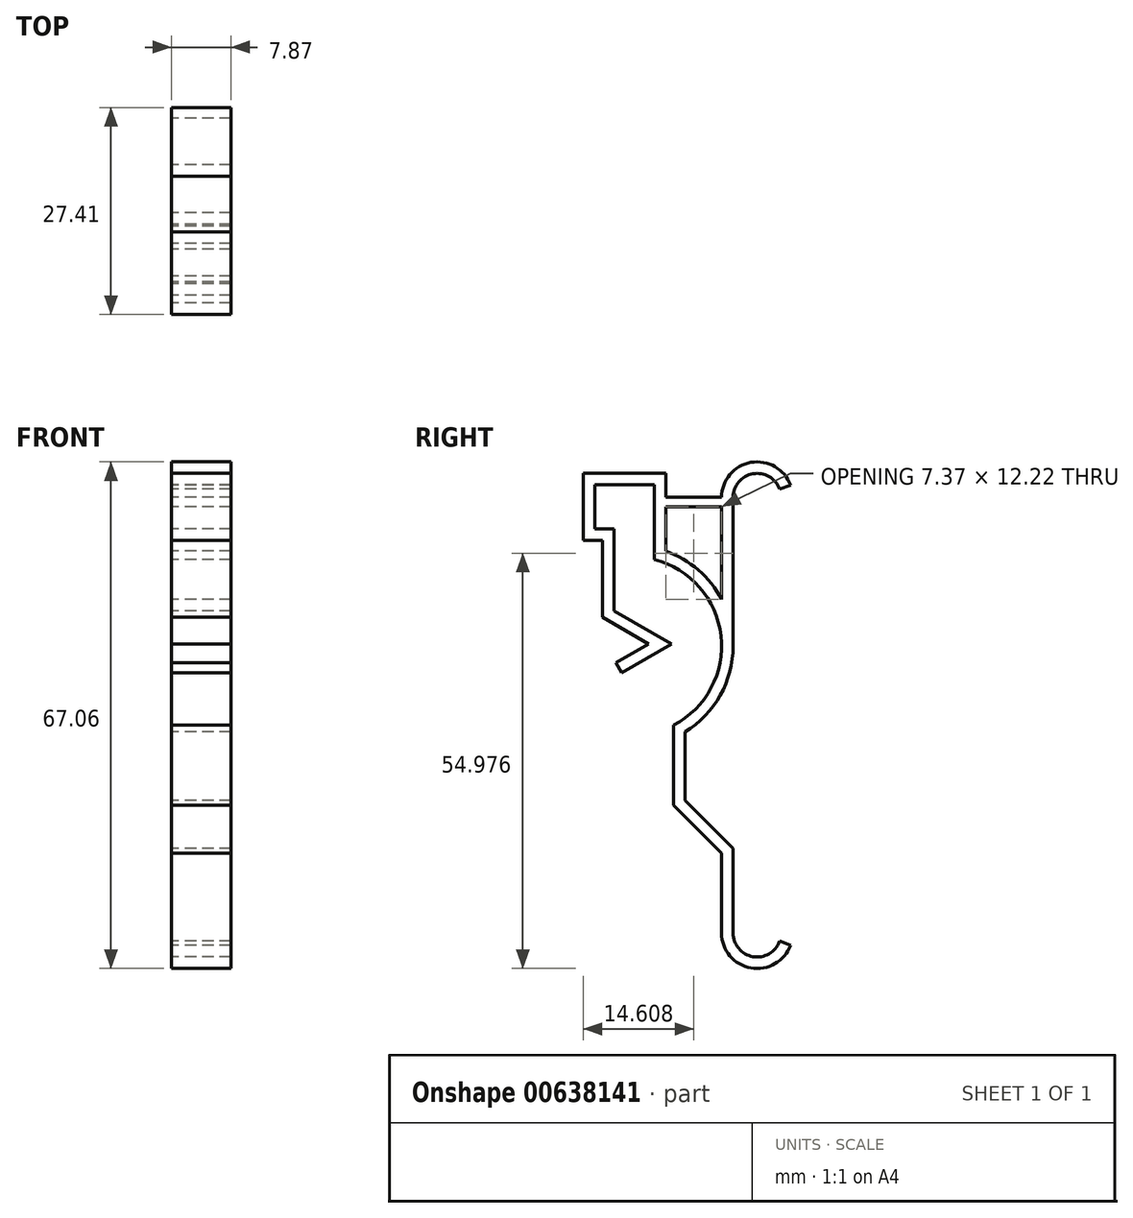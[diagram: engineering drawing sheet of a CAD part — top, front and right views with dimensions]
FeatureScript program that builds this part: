
annotation { "Feature Type Name" : "Feature", "Feature Type Description" : "" }
export const myFeature = defineFeature(function(context is Context, id is Id, definition is map)
    precondition{}
    {
        {
            var Q0;
            Q0=qCreatedBy(makeId("Right.planeOp"),FACE);
            var sketch = newSketch(context, id + "F0", { "sketchPlane" : qUnion([Q0])});
            skArc(sketch, "E0", {"start": v(-3.18, 0) * mm, "mid": v(-0.55, -3.13) * mm, "end": v(2.98, -1.09) * mm});
            skLineSegment(sketch, "E1", {"start": v(0, 0) * mm, "end": v(0, 57.66) * mm, "construction": true});
            skArc(sketch, "E2", {"start": v(2.98, 58.74) * mm, "mid": v(-0.55, 60.78) * mm, "end": v(-3.17, 57.66) * mm});
            skLineSegment(sketch, "E3", {"start": v(-3.18, 11.18) * mm, "end": v(-3.18, 0) * mm});
            skLineSegment(sketch, "E4", {"start": v(-3.17, 11.18) * mm, "end": v(-9.53, 17.53) * mm});
            skLineSegment(sketch, "E5", {"start": v(-9.53, 17.53) * mm, "end": v(-9.53, 26.61) * mm});
            skArc(sketch, "E6", {"start": v(-9.53, 26.61) * mm, "mid": v(-4.87, 31.47) * mm, "end": v(-3.18, 37.97) * mm});
            skLineSegment(sketch, "E7", {"start": v(-3.18, 37.97) * mm, "end": v(-3.18, 57.66) * mm});
            skLineSegment(sketch, "E8", {"start": v(0, -3.18) * mm, "end": v(-10.82, -3.18) * mm, "construction": true});
            skLineSegment(sketch, "E9", {"start": v(-12.07, 60.83) * mm, "end": v(-12.07, 57.66) * mm});
            skLineSegment(sketch, "E10", {"start": v(0, 60.83) * mm, "end": v(-34.51, 60.83) * mm, "construction": true});
            skLineSegment(sketch, "E11", {"start": v(-12.07, 60.83) * mm, "end": v(-22.99, 60.83) * mm});
            skLineSegment(sketch, "E12", {"start": v(-22.99, 60.83) * mm, "end": v(-22.99, 51.94) * mm});
            skLineSegment(sketch, "E13", {"start": v(-22.99, 51.94) * mm, "end": v(-20.45, 51.94) * mm});
            skLineSegment(sketch, "E14", {"start": v(-20.45, 51.94) * mm, "end": v(-20.45, 41.78) * mm});
            skLineSegment(sketch, "E15", {"start": v(0, 0) * mm, "end": v(14.09, -5.13) * mm, "construction": true});
            skLineSegment(sketch, "E16", {"start": v(0, 57.66) * mm, "end": v(12.81, 62.32) * mm, "construction": true});
            skArc(sketch, "E17.0", {"start": v(4.42, 59.27) * mm, "mid": v(-0.82, 62.29) * mm, "end": v(-4.7, 57.66) * mm});
            skArc(sketch, "E18.0", {"start": v(-4.7, 0) * mm, "mid": v(-0.82, -4.63) * mm, "end": v(4.42, -1.6) * mm});
            skLineSegment(sketch, "E19", {"start": v(2.98, -1.09) * mm, "end": v(4.42, -1.6) * mm});
            skLineSegment(sketch, "E20", {"start": v(2.98, 58.74) * mm, "end": v(4.42, 59.27) * mm});
            skLineSegment(sketch, "E21", {"start": v(-4.7, 0) * mm, "end": v(-4.7, 10.54) * mm});
            skLineSegment(sketch, "E22", {"start": v(-4.7, 10.54) * mm, "end": v(-11.05, 16.9) * mm});
            skLineSegment(sketch, "E23", {"start": v(-11.05, 16.9) * mm, "end": v(-11.05, 27.5) * mm});
            skArc(sketch, "E24.0", {"start": v(-11.05, 27.5) * mm, "mid": v(-4.78, 39.33) * mm, "end": v(-13.59, 49.42) * mm});
            skLineSegment(sketch, "E25", {"start": v(-13.59, 59.3) * mm, "end": v(-13.59, 49.42) * mm});
            skLineSegment(sketch, "E26", {"start": v(-13.59, 59.3) * mm, "end": v(-21.46, 59.3) * mm});
            skLineSegment(sketch, "E27", {"start": v(-21.46, 59.3) * mm, "end": v(-21.46, 53.47) * mm});
            skLineSegment(sketch, "E28", {"start": v(-21.46, 53.47) * mm, "end": v(-18.92, 53.47) * mm});
            skLineSegment(sketch, "E29", {"start": v(-18.92, 53.47) * mm, "end": v(-18.92, 42.66) * mm});
            skLineSegment(sketch, "E30", {"start": v(-4.7, 56.39) * mm, "end": v(-4.7, 44.16) * mm});
            skArc(sketch, "E31.trimOffspring", {"start": v(-4.7, 44.16) * mm, "mid": v(-7.78, 48.05) * mm, "end": v(-12.07, 50.55) * mm});
            skLineSegment(sketch, "E32", {"start": v(-18.92, 42.66) * mm, "end": v(-11.3, 38.26) * mm});
            skLineSegment(sketch, "E33", {"start": v(-11.3, 38.26) * mm, "end": v(-17.9, 34.45) * mm});
            skLineSegment(sketch, "E34", {"start": v(-20.45, 41.78) * mm, "end": v(-14.35, 38.26) * mm});
            skLineSegment(sketch, "E35", {"start": v(-14.35, 38.26) * mm, "end": v(-18.66, 35.77) * mm});
            skLineSegment(sketch, "E36", {"start": v(-18.66, 35.77) * mm, "end": v(-17.9, 34.45) * mm});
            skPoint(sketch, "E37.orphan", {"position": v(-20.45, 32.98) * mm});
            skLineSegment(sketch, "E38", {"start": v(-4.7, 57.66) * mm, "end": v(-12.07, 57.66) * mm});
            skLineSegment(sketch, "E39", {"start": v(-4.7, 56.39) * mm, "end": v(-12.07, 56.39) * mm});
            skLineSegment(sketch, "E40.trimOffspring", {"start": v(-12.07, 56.39) * mm, "end": v(-12.07, 50.55) * mm});
            skSolve(sketch);
        }
        {
            var Q0;
            Q0 = qSketchRegion(id + "F0", true);
            extrude(context, id + "F1", {"entities" : qUnion([Q0]), "depth" : 7.87 * mm, "offsetDistance" : 25.4 * mm});
        }
    });
